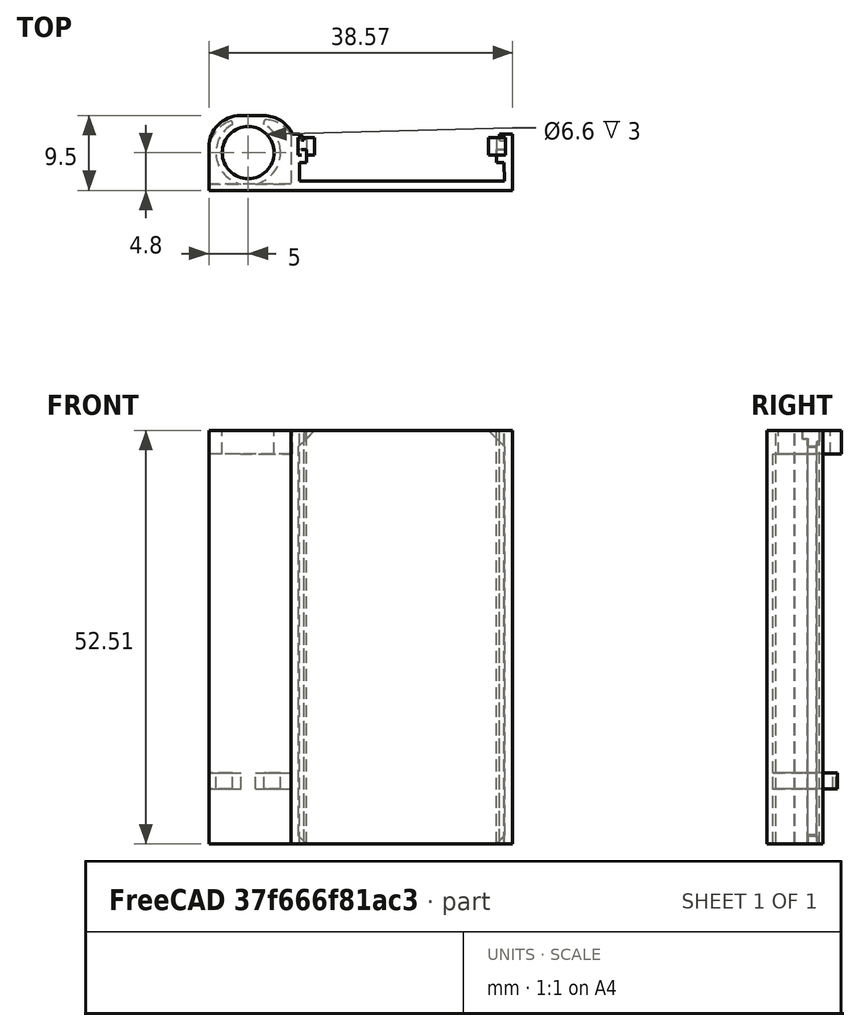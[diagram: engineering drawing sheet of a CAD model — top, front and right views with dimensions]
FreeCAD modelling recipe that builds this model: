
FCSTD DOCUMENT  (FreeCAD 0.16R)
Label: ArduinoHalter
License: All rights reserved
LicenseURL: http://en.wikipedia.org/wiki/All_rights_reserved
objects: Part::Fillet×6, Sketcher::SketchObject×5, PartDesign::Pad×5, Part::Box×4, Part::Cut×3, Part::Cylinder×2, Part::MultiFuse×1, Mesh::Feature×1
note: 31 computed .brp shape members not serialized (recipe doc carries the construction recipe); baked Part::Feature solids carry a one-line shape summary decoded from their .brp

FEATURE [Sketcher::SketchObject] Sketch
  sketch-geometry (21):
    g0: LineSegment StartX=-18.4968 StartY=-10.0088 StartZ=0 EndX=7.53504 EndY=-10.0088 EndZ=0
    g1: LineSegment StartX=8.57388 StartY=-11.2005 StartZ=0 EndX=-19.5534 EndY=-11.2005 EndZ=0
    g2: LineSegment StartX=-17.6048 StartY=-6.00567 StartZ=0 EndX=-17.6048 EndY=-7.68179 EndZ=0
    g3: LineSegment StartX=8.57269 StartY=-4.05913 StartZ=0 EndX=8.57388 EndY=-11.2005 EndZ=0
    g4: LineSegment StartX=6.91065 StartY=-4.05913 StartZ=0 EndX=6.91356 EndY=-4.85559 EndZ=0
    g5: LineSegment StartX=6.91065 StartY=-4.05913 StartZ=0 EndX=8.57269 EndY=-4.05913 EndZ=0
    g6: LineSegment StartX=6.91356 StartY=-4.85559 StartZ=0 EndX=7.6386 EndY=-4.86736 EndZ=0
    g7: LineSegment StartX=7.6386 StartY=-4.86736 StartZ=0 EndX=7.64142 EndY=-5.99166 EndZ=0
    g8: LineSegment StartX=7.64142 StartY=-5.99166 StartZ=0 EndX=6.53466 EndY=-5.99604 EndZ=0
    g9: LineSegment StartX=6.53466 StartY=-5.99604 StartZ=0 EndX=6.53538 EndY=-7.65721 EndZ=0
    g10: LineSegment StartX=-17.6048 StartY=-6.00567 StartZ=0 EndX=-18.6255 EndY=-6.00154 EndZ=0
    g11: LineSegment StartX=-18.6255 StartY=-6.00154 StartZ=0 EndX=-18.62 EndY=-4.8031 EndZ=0
    g12: LineSegment StartX=-18.62 StartY=-4.8031 StartZ=0 EndX=-17.9262 EndY=-4.80553 EndZ=0
    g13: LineSegment StartX=-17.9262 StartY=-4.80553 StartZ=0 EndX=-17.9262 EndY=-4.48409 EndZ=0
    g14: LineSegment StartX=-17.9262 StartY=-4.48409 StartZ=0 EndX=-18.4601 EndY=-4.05553 EndZ=0
    g15: LineSegment StartX=-19.5659 StartY=-4.05361 StartZ=0 EndX=-19.5534 EndY=-11.2005 EndZ=0
    g16: LineSegment StartX=-17.6048 StartY=-7.68179 StartZ=0 EndX=-18.4968 EndY=-7.686 EndZ=0
    g17: LineSegment StartX=-18.4968 StartY=-7.686 StartZ=0 EndX=-18.4968 EndY=-10.0088 EndZ=0
    g18: LineSegment StartX=7.5169 StartY=-7.64985 StartZ=0 EndX=6.53538 EndY=-7.65721 EndZ=0
    g19: LineSegment StartX=7.53504 StartY=-10.0088 StartZ=0 EndX=7.5169 EndY=-7.64985 EndZ=0
    g20: LineSegment StartX=-19.5659 StartY=-4.05361 StartZ=0 EndX=-18.4601 EndY=-4.05553 EndZ=0
  constraints (24):
    c: Horizontal(g0)
    c: Horizontal(g1)
    c: Vertical(g2)
    c: Coincident(g1,g3)
    c: Coincident(g5,g4)
    c: Coincident(g4,g6)
    c: Coincident(g6,g7)
    c: Coincident(g7,g8)
    c: Coincident(g9,g8)
    c: Coincident(g5,g3)
    c: Coincident(g10,g2)
    c: Coincident(g10,g11)
    c: Coincident(g11,g12)
    c: Coincident(g12,g13)
    c: Coincident(g13,g14)
    c: Coincident(g15,g1)
    c: Coincident(g16,g2)
    c: Coincident(g16,g17)
    c: Coincident(g0,g17)
    c: Coincident(g9,g18)
    c: Coincident(g18,g19)
    c: Coincident(g0,g19)
    c: Coincident(g20,g15)
    c: Coincident(g20,g14)
FEATURE [PartDesign::Pad] Pad
  Length = 52.5
  Length2 = 100
  Sketch = -> Sketch
  Type = 0
FEATURE [Sketcher::SketchObject] Sketch004
  Placement = pos=(-11.64,-4.5,6.03) rot=(1,0,0;1.5708rad)
  sketch-geometry (3):
    g0: LineSegment StartX=-7.00166 StartY=-5.01077 StartZ=0 EndX=-6.98953 EndY=-6.02972 EndZ=0
    g1: LineSegment StartX=-6.98953 StartY=-6.02972 StartZ=0 EndX=-5.96627 EndY=-6.02972 EndZ=0
    g2: LineSegment StartX=-7.00166 StartY=-5.01077 StartZ=0 EndX=-5.96627 EndY=-6.02972 EndZ=0
  constraints (3):
    c: Coincident(g0,g1)
    c: Coincident(g2,g0)
    c: Coincident(g2,g1)
FEATURE [PartDesign::Pad] Pad004  label="stopper002"
  Length = 2.2
  Length2 = 100
  Placement = pos=(-11.64,-4.5,6.03) rot=(1,0,0;1.5708rad)
  Sketch = -> Sketch004
  Type = 0
FEATURE [Sketcher::SketchObject] Sketch006
  Placement = pos=(7.7,-4.5,0.03) rot=(1,0,0;1.5708rad)
  sketch-geometry (3):
    g0: LineSegment StartX=-0.009992 StartY=1.14657 StartZ=0 EndX=-0.005347 EndY=-0.027131 EndZ=0
    g1: LineSegment StartX=-0.005347 StartY=-0.027131 StartZ=0 EndX=-1.16636 EndY=-0.03134 EndZ=0
    g2: LineSegment StartX=-1.16636 StartY=-0.03134 StartZ=0 EndX=-0.009992 EndY=1.14657 EndZ=0
  constraints (3):
    c: Coincident(g0,g1)
    c: Coincident(g1,g2)
    c: Coincident(g2,g0)
FEATURE [PartDesign::Pad] Pad006  label="stopper003"
  Length = 2.2
  Length2 = 100
  Placement = pos=(7.7,-4.5,0.03) rot=(1,0,0;1.5708rad)
  Sketch = -> Sketch006
  Type = 0
FEATURE [Sketcher::SketchObject] Sketch007
  Placement = pos=(7.66,-4.5,50.5) rot=(1,0,0;1.5708rad)
  sketch-geometry (3):
    g0: LineSegment StartX=0.006942 StartY=2.00104 StartZ=0 EndX=-0.00277 EndY=-0.125835 EndZ=0
    g1: LineSegment StartX=-0.00277 StartY=-0.125835 StartZ=0 EndX=-2.12965 EndY=2.01075 EndZ=0
    g2: LineSegment StartX=-2.12965 StartY=2.01075 StartZ=0 EndX=0.006942 EndY=2.00104 EndZ=0
  constraints (3):
    c: Coincident(g0,g1)
    c: Coincident(g1,g2)
    c: Coincident(g2,g0)
FEATURE [Sketcher::SketchObject] Sketch008
  Placement = pos=(-17.65,-4.5,50.5) rot=(1,0,0;1.5708rad)
  sketch-geometry (3):
    g0: LineSegment StartX=1.0898 StartY=1.99523 StartZ=0 EndX=-0.993398 EndY=-0.061924 EndZ=0
    g1: LineSegment StartX=-0.993398 StartY=-0.061924 StartZ=0 EndX=-0.997928 EndY=2.00119 EndZ=0
    g2: LineSegment StartX=-0.997928 StartY=2.00119 StartZ=0 EndX=1.0898 EndY=1.99523 EndZ=0
  constraints (3):
    c: Coincident(g0,g1)
    c: Coincident(g1,g2)
    c: Coincident(g2,g0)
FEATURE [PartDesign::Pad] Pad008  label="stopper001"
  Length = 2.2
  Length2 = 100
  Placement = pos=(-17.65,-4.5,50.5) rot=(1,0,0;1.5708rad)
  Sketch = -> Sketch008
  Type = 0
FEATURE [Part::Box] Box002  label="Würfel"
  Height = 2
  Length = 11
  Placement = pos=(-30,-11,7) rot=(0,0,1;0rad)
  Width = 9
FEATURE [Part::Cylinder] Cylinder  label="Zylinder"
  Angle = 360
  Height = 10
  Placement = pos=(-25,-6.2,0) rot=(0,0,1;0rad)
  Radius = 4.1
FEATURE [Part::Cut] Cut002
  Base = -> Box002
  Tool = -> Cylinder
FEATURE [Part::Fillet] Fillet002
  Base = -> Cut002
  Edges = 1 edges r=4: [Edge12]
FEATURE [Part::Fillet] Fillet003  label="Antenne001"
  Base = -> Fillet002
  Edges = 1 edges r=4: [Edge9]
  Placement = pos=(0,-0.2,0) rot=(0,0,1;0rad)
FEATURE [PartDesign::Pad] Pad007  label="stopper004"
  Length = 2.2
  Length2 = 100
  Placement = pos=(7.66,-4.5,50.5) rot=(1,0,0;1.5708rad)
  Sketch = -> Sketch007
  Type = 0
FEATURE [Part::Box] Box003  label="Würfel001"
  Height = 3
  Length = 11
  Placement = pos=(-30,-11,7) rot=(0,0,1;0rad)
  Width = 9.5
FEATURE [Part::Cylinder] Cylinder001  label="Zylinder001"
  Angle = 360
  Height = 10
  Placement = pos=(-25,-6.2,0) rot=(0,0,1;0rad)
  Radius = 3.3
FEATURE [Part::Cut] Cut003
  Base = -> Box003
  Placement = pos=(0,0,42.5) rot=(0,0,1;0rad)
  Tool = -> Cylinder001
FEATURE [Part::Fillet] Fillet004
  Base = -> Cut003
  Edges = 1 edges r=4: [Edge12]
FEATURE [Part::Fillet] Fillet005  label="Antenne002"
  Base = -> Fillet004
  Edges = 1 edges r=4: [Edge9]
  Placement = pos=(0,-0.2,0) rot=(0,0,1;0rad)
FEATURE [Part::Box] Box  label="AntenneBoden"
  Height = 50
  Length = 11
  Placement = pos=(-30,-11.2,0) rot=(0,0,1;0rad)
  Width = 0.8
FEATURE [Part::Box] Box004  label="Würfel003"
  Height = 3
  Length = 4
  Placement = pos=(-27,-4,6.5) rot=(0,0,1;0rad)
  Width = 3
FEATURE [Part::Cut] Cut
  Base = -> Fillet003
  Tool = -> Box004
FEATURE [Part::Fillet] Fillet
  Base = -> Cut
  Edges = 1 edges r=0.2: [Edge19]
FEATURE [Part::Fillet] Fillet006  label="Antenne003"
  Base = -> Fillet
  Edges = 1 edges r=0.3: [Edge29]
FEATURE [Part::MultiFuse] Fusion
  Shapes = -> [Pad,Fillet005,Pad004,Pad006,Pad008,Pad007,Box,Fillet006]
FEATURE [Mesh::Feature] Mesh  label="Fusion (Meshed)"
